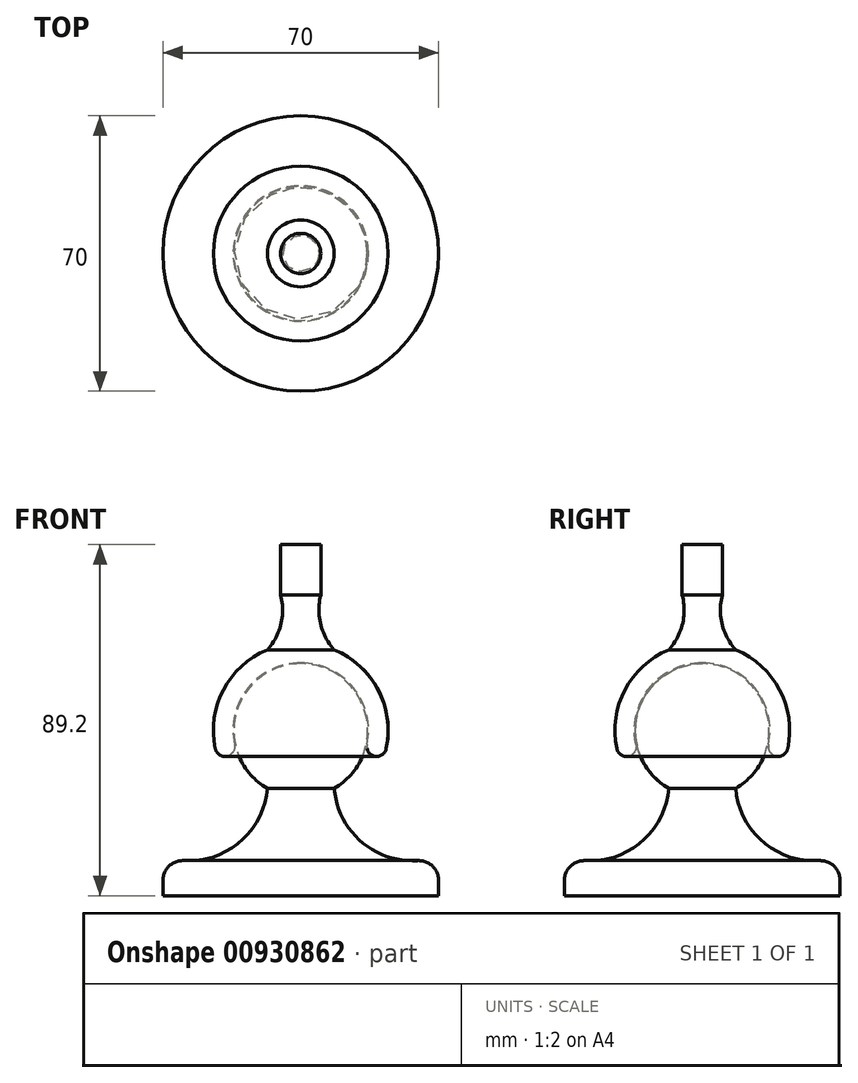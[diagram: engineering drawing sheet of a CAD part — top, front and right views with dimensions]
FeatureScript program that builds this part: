
annotation { "Feature Type Name" : "Feature", "Feature Type Description" : "" }
export const myFeature = defineFeature(function(context is Context, id is Id, definition is map)
    precondition{}
    {
        {
            var Q0;
            Q0=qCreatedBy(makeId("Right.planeOp"),FACE);
            var sketch = newSketch(context, id + "F0", { "sketchPlane" : qUnion([Q0])});
            skLineSegment(sketch, "E0", {"start": v(0, 0) * mm, "end": v(-35, 0) * mm});
            skLineSegment(sketch, "E1", {"start": v(-35, 0) * mm, "end": v(-35, 10) * mm});
            skLineSegment(sketch, "E2", {"start": v(0, 10) * mm, "end": v(0, 25) * mm, "construction": true});
            skArc(sketch, "E3", {"start": v(0, 59) * mm, "mid": v(-17, 42) * mm, "end": v(0, 25) * mm});
            skArc(sketch, "E4", {"start": v(-35, 10) * mm, "mid": v(-17.51, 12.14) * mm, "end": v(-8.5, 27.28) * mm});
            skLineSegment(sketch, "E5", {"start": v(-17, -67.07) * mm, "end": v(-17, 133.38) * mm, "construction": true});
            skPoint(sketch, "E5.startSnap0", {"position": v(-17, 42) * mm});
            skLineSegment(sketch, "E6", {"start": v(-17, 133.38) * mm, "end": v(0, 133.38) * mm, "construction": true});
            skLineSegment(sketch, "E7", {"start": v(-8.5, -58.54) * mm, "end": v(-8.5, 133.38) * mm, "construction": true});
            skPoint(sketch, "E7.startSnap0", {"position": v(-8.5, 133.38) * mm});
            skPoint(sketch, "E7.endSnap0", {"position": v(-8.5, 133.38) * mm});
            skLineSegment(sketch, "E8", {"start": v(0, 42) * mm, "end": v(-35.72, 42) * mm, "construction": true});
            skLineSegment(sketch, "E9", {"start": v(0, 42) * mm, "end": v(-37.8, 33.97) * mm, "construction": true});
            skLineSegment(sketch, "E10", {"start": v(0, 59) * mm, "end": v(0, 59.2) * mm, "construction": true});
            skArc(sketch, "E11", {"start": v(0, 59.2) * mm, "mid": v(-13.37, 52.82) * mm, "end": v(-16.82, 38.42) * mm});
            skArc(sketch, "E12.0", {"start": v(0, 64.2) * mm, "mid": v(-17.25, 55.97) * mm, "end": v(-21.71, 37.38) * mm});
            skLineSegment(sketch, "E13", {"start": v(-21.71, 37.38) * mm, "end": v(-16.82, 38.42) * mm});
            skArc(sketch, "E14", {"start": v(-21.71, 37.38) * mm, "mid": v(-18.75, 35.46) * mm, "end": v(-16.82, 38.42) * mm});
            skLineSegment(sketch, "E15", {"start": v(0, 59) * mm, "end": v(0, 0) * mm});
            skLineSegment(sketch, "E16", {"start": v(0, 64.2) * mm, "end": v(0, 59.2) * mm});
            skLineSegment(sketch, "E17", {"start": v(0, 89.2) * mm, "end": v(0, 64.2) * mm});
            skLineSegment(sketch, "E18", {"start": v(-5.1, 63.6) * mm, "end": v(-5.1, 89.2) * mm});
            skLineSegment(sketch, "E19", {"start": v(0, 89.2) * mm, "end": v(-5.1, 89.2) * mm});
            skArc(sketch, "E20", {"start": v(-8.5, 62.5) * mm, "mid": v(-5.04, 69.02) * mm, "end": v(-5.1, 76.4) * mm});
            skSolve(sketch);
        }
        {
            var Q0;
            {var subQ4=sQuery(id+"F0.wireOp",EDGE,"E0");Q0=makeQuery(id+"F0.imprint","IMPRINT",FACE,{"disambiguationData":[TD([[makeQuery(id+"F0.imprint","IMPRINT",EDGE,{"derivedFrom":subQ4}),-1.0]])]});}
            var Q1;
            {var subQ0=sQuery(id+"F0.wireOp",EDGE,"E15");var subQ1=sQuery(id+"F0.wireOp",EDGE,"E3");var subQ2=makeQuery(id+"F0.imprint","INTERSECT",VERTEX,{"disambiguationData":[OD(0.0)],"derivedFrom":[subQ1,subQ0]});Q1=makeQuery(id+"F0.imprint","IMPRINT",FACE,{"disambiguationData":[TD([[makeQuery(id+"F0.imprint","IMPRINT",EDGE,{"disambiguationData":[TD([[subQ2,-1.0]])],"derivedFrom":subQ1}),1.0]])]});}
            var Q2;
            Q2=sQuery(id+"F0.wireOp",EDGE,"E15");
            revolve(context, id + "F1", {"surfaceOperationType" : NewSurfaceOperationType.NEW, "entities" : qUnion([Q0, Q1]), "axis" : qUnion([Q2]), "revolveType" : RevolveType.FULL});
        }
        {
            var Q0;
            Q0=makeQuery(id+"F0.imprint","IMPRINT",FACE,{"disambiguationData":[TD([[makeQuery(id+"F0.imprint","IMPRINT",EDGE,{"derivedFrom":sQuery(id+"F0.wireOp",EDGE,"E11")}),-1.0]])]});
            var Q1;
            {var subQ0=sQuery(id+"F0.wireOp",EDGE,"E18");var subQ1=sQuery(id+"F0.wireOp",EDGE,"E12.0");var subQ2=makeQuery(id+"F0.imprint","INTERSECT",VERTEX,{"derivedFrom":[subQ1,subQ0]});Q1=makeQuery(id+"F0.imprint","IMPRINT",FACE,{"disambiguationData":[TD([[makeQuery(id+"F0.imprint","IMPRINT",EDGE,{"disambiguationData":[TD([[subQ2,-1.0]])],"derivedFrom":subQ1}),-1.0]])]});}
            var Q2;
            {var subQ4=sQuery(id+"F0.wireOp",EDGE,"E17");Q2=makeQuery(id+"F0.imprint","IMPRINT",FACE,{"disambiguationData":[TD([[makeQuery(id+"F0.imprint","IMPRINT",EDGE,{"derivedFrom":subQ4}),-1.0]])]});}
            var Q3;
            Q3=makeQuery(id+"F0.imprint","IMPRINT",FACE,{"disambiguationData":[TD([[makeQuery(id+"F0.imprint","IMPRINT",EDGE,{"derivedFrom":sQuery(id+"F0.wireOp",EDGE,"E13")}),-1.0]])]});
            var Q4;
            Q4=sQuery(id+"F0.wireOp",EDGE,"E17");
            revolve(context, id + "F2", {"surfaceOperationType" : NewSurfaceOperationType.NEW, "entities" : qUnion([Q0, Q1, Q2, Q3]), "axis" : qUnion([Q4]), "revolveType" : RevolveType.FULL});
        }
        {
            var Q0;
            Q0=makeQuery(id+"F1.opRevolve","SWEPT_EDGE",EDGE,{"disambiguationData":[OSD([sQuery(id+"F0.wireOp",EDGE,"E1"),sQuery(id+"F0.wireOp",EDGE,"E4")])]});
            fillet(context, id + "F3", {"entities" : qUnion([Q0]), "radius" : 5 * mm, "tangentPropagation" : true, "allowEdgeOverflow" : false});
        }
    });
